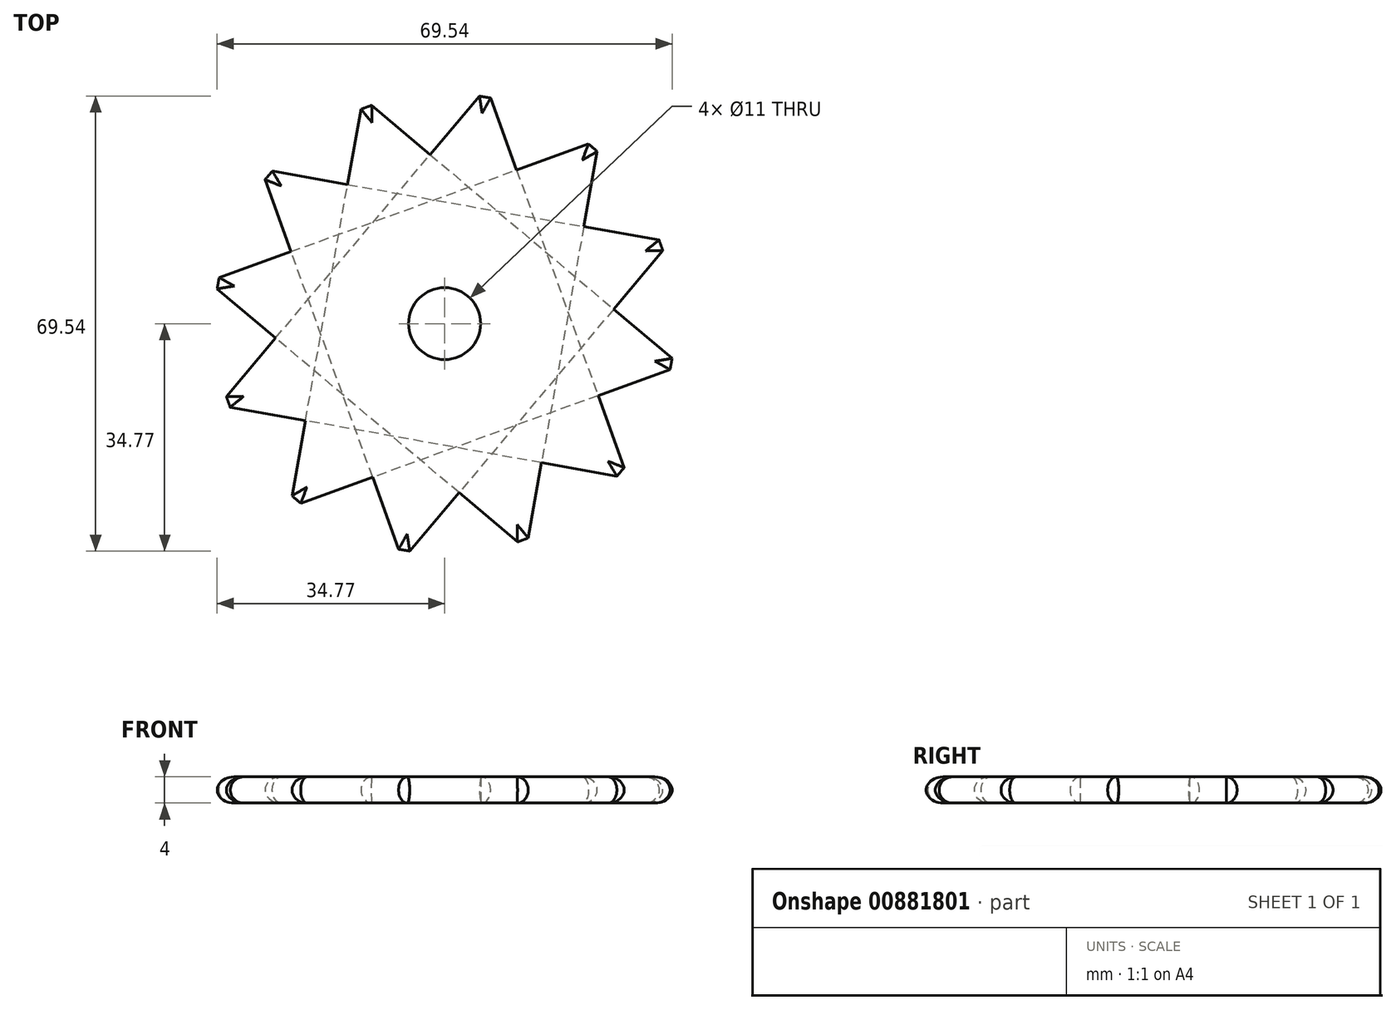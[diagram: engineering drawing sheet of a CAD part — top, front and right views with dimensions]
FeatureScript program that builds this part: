
annotation { "Feature Type Name" : "Feature", "Feature Type Description" : "" }
export const myFeature = defineFeature(function(context is Context, id is Id, definition is map)
    precondition{}
    {
        {
            var Q0;
            Q0=qCreatedBy(makeId("Top.planeOp"),FACE);
            var sketch = newSketch(context, id + "F0", { "sketchPlane" : qUnion([Q0])});
            skCircle(sketch, "E0.cCircle", {"center": v(0, 0) * mm, "radius": 18.33 * mm, "construction": true});
            skLineSegment(sketch, "E0.0", {"start": v(-23.62, -28.04) * mm, "end": v(-12.47, 34.48) * mm});
            skLineSegment(sketch, "E0.1", {"start": v(-12.47, 34.48) * mm, "end": v(36.1, -6.44) * mm});
            skLineSegment(sketch, "E0.2", {"start": v(36.1, -6.44) * mm, "end": v(-23.62, -28.04) * mm});
            skPoint(sketch, "E0.0.midPoint", {"position": v(-18.05, 3.22) * mm});
            skCircle(sketch, "E1", {"center": v(0, 0) * mm, "radius": 5.5 * mm});
            skSolve(sketch);
        }
        {
            var Q0;
            Q0=makeQuery(id+"F0.imprint","IMPRINT",FACE,{"disambiguationData":[TD([[makeQuery(id+"F0.imprint","IMPRINT",EDGE,{"derivedFrom":sQuery(id+"F0.wireOp",EDGE,"E0.0")}),-1.0]])]});
            extrude(context, id + "F1", {"entities" : qUnion([Q0]), "depth" : 4 * mm, "offsetDistance" : 25 * mm});
        }
        {
            var Q0;
            Q0=makeQuery(id+"F1.opExtrude","CAP_EDGE",EDGE,{"disambiguationData":[OSD([sQuery(id+"F0.wireOp",EDGE,"E0.0")])],"isStart":false});
            var Q1;
            Q1=makeQuery(id+"F1.opExtrude","CAP_EDGE",EDGE,{"disambiguationData":[OSD([sQuery(id+"F0.wireOp",EDGE,"E0.1")])],"isStart":false});
            var Q2;
            Q2=makeQuery(id+"F1.opExtrude","CAP_EDGE",EDGE,{"disambiguationData":[OSD([sQuery(id+"F0.wireOp",EDGE,"E0.2")])],"isStart":false});
            var Q3;
            Q3=makeQuery(id+"F1.opExtrude","CAP_EDGE",EDGE,{"disambiguationData":[OSD([sQuery(id+"F0.wireOp",EDGE,"E0.1")])],"isStart":true});
            var Q4;
            Q4=makeQuery(id+"F1.opExtrude","CAP_EDGE",EDGE,{"disambiguationData":[OSD([sQuery(id+"F0.wireOp",EDGE,"E0.0")])],"isStart":true});
            var Q5;
            Q5=makeQuery(id+"F1.opExtrude","CAP_EDGE",EDGE,{"disambiguationData":[OSD([sQuery(id+"F0.wireOp",EDGE,"E0.2")])],"isStart":true});
            fillet(context, id + "F2", {"entities" : qUnion([Q0, Q1, Q2, Q3, Q4, Q5]), "radius" : 2 * mm, "tangentPropagation" : true, "allowEdgeOverflow" : false});
        }
        {
            var Q0;
            Q0=makeQuery(id+"F2.opFillet","BLEND_EDGE",EDGE,{"blendedFrom":[makeQuery(id+"F1.opExtrude","CAP_EDGE",EDGE,{"disambiguationData":[OSD([sQuery(id+"F0.wireOp",EDGE,"E0.0")])],"isStart":true}),makeQuery(id+"F1.opExtrude","CAP_EDGE",EDGE,{"disambiguationData":[OSD([sQuery(id+"F0.wireOp",EDGE,"E0.2")])],"isStart":true})],"blendedInto":[]});
            var Q1;
            Q1=makeQuery(id+"F2.opFillet","BLEND_EDGE",EDGE,{"blendedFrom":[makeQuery(id+"F1.opExtrude","CAP_EDGE",EDGE,{"disambiguationData":[OSD([sQuery(id+"F0.wireOp",EDGE,"E0.1")])],"isStart":true}),makeQuery(id+"F1.opExtrude","CAP_EDGE",EDGE,{"disambiguationData":[OSD([sQuery(id+"F0.wireOp",EDGE,"E0.2")])],"isStart":true})],"blendedInto":[]});
            var Q2;
            Q2=makeQuery(id+"F2.opFillet","BLEND_EDGE",EDGE,{"blendedFrom":[makeQuery(id+"F1.opExtrude","CAP_EDGE",EDGE,{"disambiguationData":[OSD([sQuery(id+"F0.wireOp",EDGE,"E0.0")])],"isStart":true}),makeQuery(id+"F1.opExtrude","CAP_EDGE",EDGE,{"disambiguationData":[OSD([sQuery(id+"F0.wireOp",EDGE,"E0.1")])],"isStart":true})],"blendedInto":[]});
            chamfer(context, id + "F3", {"entities" : qUnion([Q0, Q1, Q2]), "width" : 1 * mm, "tangentPropagation" : true});
        }
        {
            var Q0;
            Q0=makeQuery(id+"F1.opExtrude","SWEPT_BODY",BODY,{"disambiguationData":[OSD([sQuery(id+"F0.wireOp",EDGE,"E0.0"),sQuery(id+"F0.wireOp",EDGE,"E0.1"),sQuery(id+"F0.wireOp",EDGE,"E0.2"),sQuery(id+"F0.wireOp",EDGE,"E1")])]});
            var Q1;
            Q1=makeQuery(id+"F1.opExtrude","CAP_EDGE",EDGE,{"disambiguationData":[OSD([sQuery(id+"F0.wireOp",EDGE,"E1")])],"isStart":false});
            circularPattern(context, id + "F4", {"entities" : qUnion([Q0]), "axis" : qUnion([Q1]), "angle" : 90 * degree, "instanceCount" : 4, "equalSpace" : true});
        }
    });
